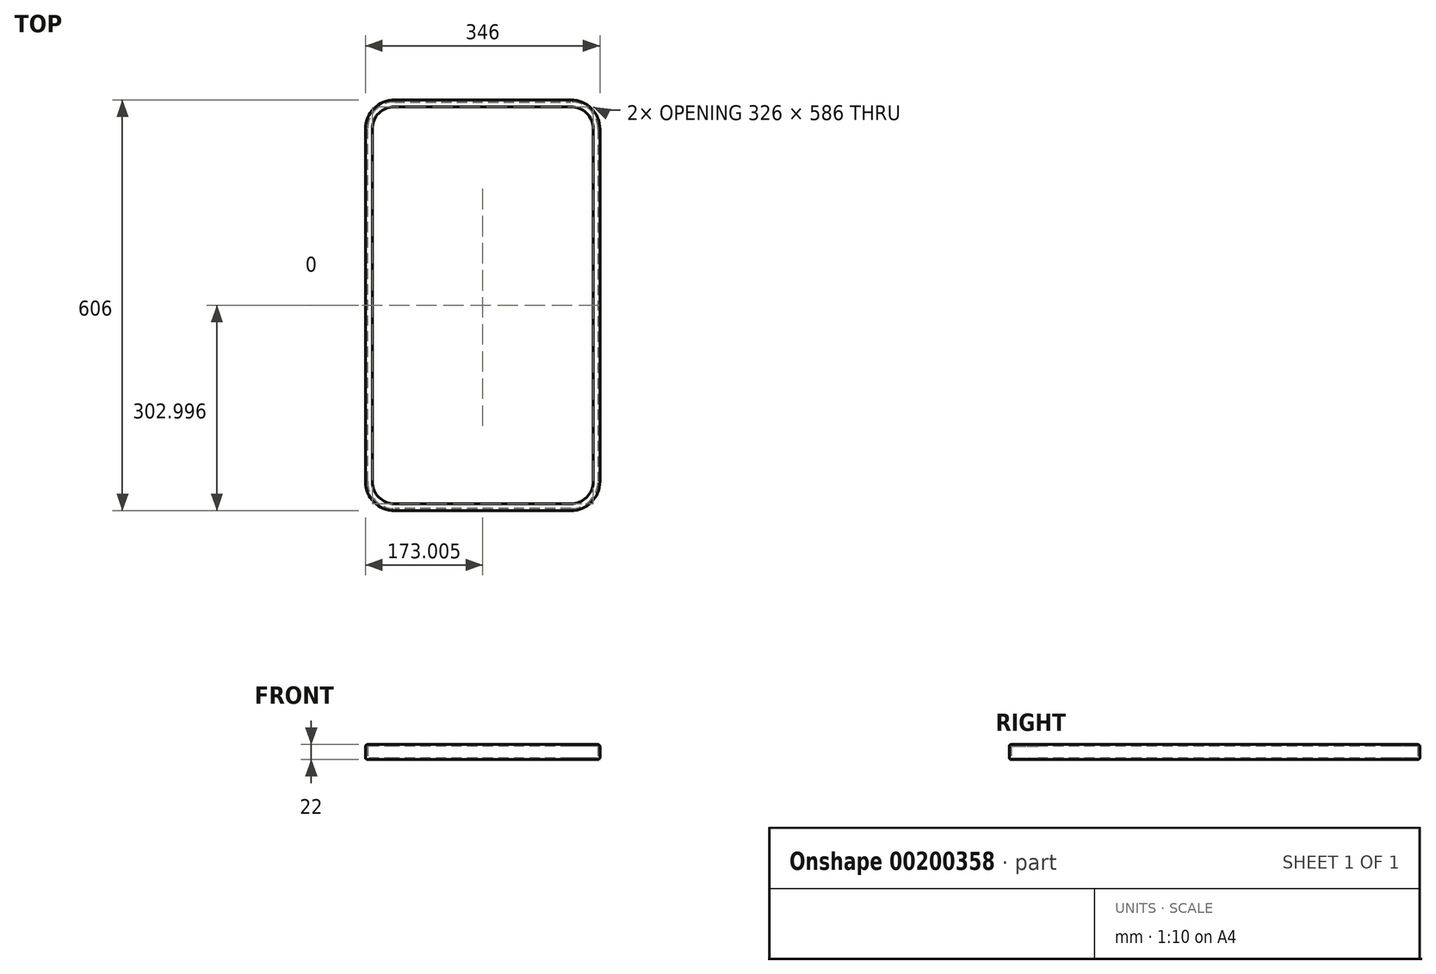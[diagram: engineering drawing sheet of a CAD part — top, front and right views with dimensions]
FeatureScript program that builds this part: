
annotation { "Feature Type Name" : "Feature", "Feature Type Description" : "" }
export const myFeature = defineFeature(function(context is Context, id is Id, definition is map)
    precondition{}
    {
        {
            var Q0;
            Q0=qCreatedBy(makeId("Top.planeOp"),FACE);
            var sketch = newSketch(context, id + "F0", { "sketchPlane" : qUnion([Q0])});
            skLineSegment(sketch, "E0.bottom", {"start": v(285.61, -73.6) * mm, "end": v(25.61, -73.6) * mm});
            skLineSegment(sketch, "E0.top", {"start": v(285.61, 526.4) * mm, "end": v(25.61, 526.4) * mm});
            skLineSegment(sketch, "E0.left", {"start": v(325.61, -33.6) * mm, "end": v(325.61, 486.4) * mm});
            skLineSegment(sketch, "E0.right", {"start": v(-14.39, -33.6) * mm, "end": v(-14.39, 486.4) * mm});
            skPoint(sketch, "E1.visualSharp", {"position": v(-14.39, -73.6) * mm});
            skArc(sketch, "E1.filletArc", {"start": v(-14.39, -33.6) * mm, "mid": v(-2.67, -61.88) * mm, "end": v(25.61, -73.6) * mm});
            skPoint(sketch, "E2.visualSharp", {"position": v(325.61, -73.6) * mm});
            skArc(sketch, "E2.filletArc", {"start": v(285.61, -73.6) * mm, "mid": v(313.9, -61.88) * mm, "end": v(325.61, -33.6) * mm});
            skPoint(sketch, "E3.visualSharp", {"position": v(325.61, 526.4) * mm});
            skArc(sketch, "E3.filletArc", {"start": v(325.61, 486.4) * mm, "mid": v(313.9, 514.69) * mm, "end": v(285.61, 526.4) * mm});
            skPoint(sketch, "E4.visualSharp", {"position": v(-14.39, 526.4) * mm});
            skArc(sketch, "E4.filletArc", {"start": v(25.61, 526.4) * mm, "mid": v(-2.67, 514.69) * mm, "end": v(-14.39, 486.4) * mm});
            skSolve(sketch);
        }
        {
            var Q0;
            Q0 = qSketchRegion(id + "F0", true);
            extrude(context, id + "F1", {"entities" : qUnion([Q0]), "depth" : 18 * mm});
        }
        {
            var Q0;
            Q0=makeQuery(id+"F1.opExtrude","CAP_VERTEX",VERTEX,{"disambiguationData":[OSD([sQuery(id+"F0.wireOp",EDGE,"E0.right"),sQuery(id+"F0.wireOp",EDGE,"E1.filletArc")])],"isStart":false});
            var Q1;
            Q1=makeQuery(id+"F1.opExtrude","CAP_VERTEX",VERTEX,{"disambiguationData":[OSD([sQuery(id+"F0.wireOp",EDGE,"E0.right"),sQuery(id+"F0.wireOp",EDGE,"E1.filletArc")])],"isStart":true});
            var Q2;
            Q2=makeQuery(id+"F1.opExtrude","CAP_VERTEX",VERTEX,{"disambiguationData":[OSD([sQuery(id+"F0.wireOp",EDGE,"E0.left"),sQuery(id+"F0.wireOp",EDGE,"E2.filletArc")])],"isStart":true});
            cPlane(context, id + "F2", {"entities" : qUnion([Q0, Q1, Q2]), "cplaneType" : CPlaneType.THREE_POINT, "offset" : 35 * mm, "width" : 150 * mm, "height" : 150 * mm});
        }
        {
            var Q0;
            Q0=qCreatedBy(id+"F2.planeOp",FACE);
            var sketch = newSketch(context, id + "F3", { "sketchPlane" : qUnion([Q0])});
            skPoint(sketch, "E5.0", {"position": v(14.39, 18) * mm});
            skPoint(sketch, "E6.0", {"position": v(14.39, 0) * mm});
            skLineSegment(sketch, "E7", {"start": v(14.39, 18) * mm, "end": v(7.39, 18) * mm});
            skLineSegment(sketch, "E8", {"start": v(7.39, 18) * mm, "end": v(7.39, 20) * mm});
            skLineSegment(sketch, "E9", {"start": v(7.39, 20) * mm, "end": v(14.39, 20) * mm});
            skLineSegment(sketch, "E10", {"start": v(17.39, 17) * mm, "end": v(17.39, 1) * mm});
            skLineSegment(sketch, "E11", {"start": v(14.39, -2) * mm, "end": v(7.39, -2) * mm});
            skLineSegment(sketch, "E12", {"start": v(7.39, -2) * mm, "end": v(7.39, 0) * mm});
            skLineSegment(sketch, "E13", {"start": v(7.39, 0) * mm, "end": v(14.39, 0) * mm});
            skLineSegment(sketch, "E14", {"start": v(14.39, 18) * mm, "end": v(14.39, 0) * mm});
            skPoint(sketch, "E15.visualSharp", {"position": v(17.39, 20) * mm});
            skArc(sketch, "E15.filletArc", {"start": v(17.39, 17) * mm, "mid": v(16.5, 19.12) * mm, "end": v(14.39, 20) * mm});
            skPoint(sketch, "E16.visualSharp", {"position": v(17.39, -2) * mm});
            skArc(sketch, "E16.filletArc", {"start": v(14.39, -2) * mm, "mid": v(16.5, -1.12) * mm, "end": v(17.39, 1) * mm});
            skSolve(sketch);
        }
        {
            var Q0;
            Q0 = qSketchRegion(id + "F3", true);
            var Q1;
            Q1=makeQuery(id+"F1.opExtrude","CAP_EDGE",EDGE,{"disambiguationData":[OSD([sQuery(id+"F0.wireOp",EDGE,"E0.right")])],"isStart":false});
            var Q2;
            Q2=makeQuery(id+"F1.opExtrude","CAP_EDGE",EDGE,{"disambiguationData":[OSD([sQuery(id+"F0.wireOp",EDGE,"E4.filletArc")])],"isStart":false});
            var Q3;
            Q3=makeQuery(id+"F1.opExtrude","CAP_EDGE",EDGE,{"disambiguationData":[OSD([sQuery(id+"F0.wireOp",EDGE,"E0.top")])],"isStart":false});
            var Q4;
            Q4=makeQuery(id+"F1.opExtrude","CAP_EDGE",EDGE,{"disambiguationData":[OSD([sQuery(id+"F0.wireOp",EDGE,"E3.filletArc")])],"isStart":false});
            var Q5;
            Q5=makeQuery(id+"F1.opExtrude","CAP_EDGE",EDGE,{"disambiguationData":[OSD([sQuery(id+"F0.wireOp",EDGE,"E0.left")])],"isStart":false});
            var Q6;
            Q6=makeQuery(id+"F1.opExtrude","CAP_EDGE",EDGE,{"disambiguationData":[OSD([sQuery(id+"F0.wireOp",EDGE,"E2.filletArc")])],"isStart":false});
            var Q7;
            Q7=makeQuery(id+"F1.opExtrude","CAP_EDGE",EDGE,{"disambiguationData":[OSD([sQuery(id+"F0.wireOp",EDGE,"E0.bottom")])],"isStart":false});
            var Q8;
            Q8=makeQuery(id+"F1.opExtrude","CAP_EDGE",EDGE,{"disambiguationData":[OSD([sQuery(id+"F0.wireOp",EDGE,"E1.filletArc")])],"isStart":false});
            sweep(context, id + "F4", {"profiles" : qUnion([Q0]), "path" : qUnion([Q1, Q2, Q3, Q4, Q5, Q6, Q7, Q8])});
        }
    });
